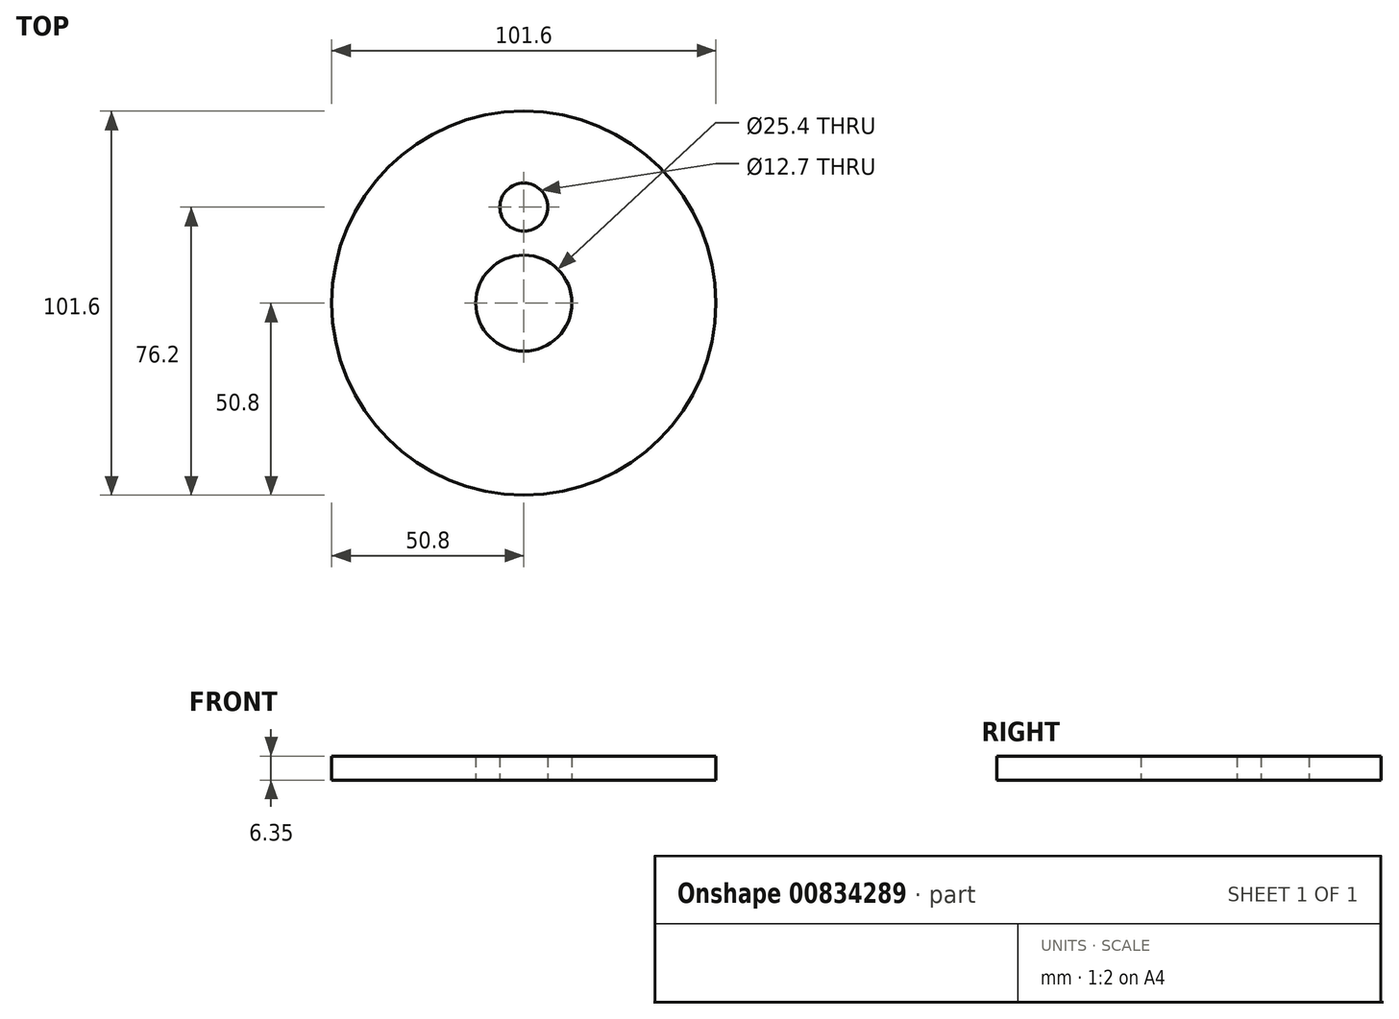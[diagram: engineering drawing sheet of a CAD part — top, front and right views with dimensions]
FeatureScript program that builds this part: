
annotation { "Feature Type Name" : "Feature", "Feature Type Description" : "" }
export const myFeature = defineFeature(function(context is Context, id is Id, definition is map)
    precondition{}
    {
        {
            var Q0;
            Q0=qCreatedBy(makeId("Top.planeOp"),FACE);
            var sketch = newSketch(context, id + "F0", { "sketchPlane" : qUnion([Q0])});
            skCircle(sketch, "E0", {"center": v(0, 0) * mm, "radius": 50.8 * mm});
            skCircle(sketch, "E1", {"center": v(0, 0) * mm, "radius": 12.7 * mm});
            skLineSegment(sketch, "E2", {"start": v(0, 0) * mm, "end": v(0, 50.8) * mm, "construction": true});
            skCircle(sketch, "E3", {"center": v(0, 25.4) * mm, "radius": 6.35 * mm});
            skSolve(sketch);
        }
        {
            var Q0;
            Q0=makeQuery(id+"F0.imprint","IMPRINT",FACE,{"disambiguationData":[TD([[makeQuery(id+"F0.imprint","IMPRINT",EDGE,{"derivedFrom":sQuery(id+"F0.wireOp",EDGE,"E0")}),1.0]])]});
            extrude(context, id + "F1", {"entities" : qUnion([Q0]), "depth" : 6.35 * mm, "offsetDistance" : 25.4 * mm});
        }
    });
